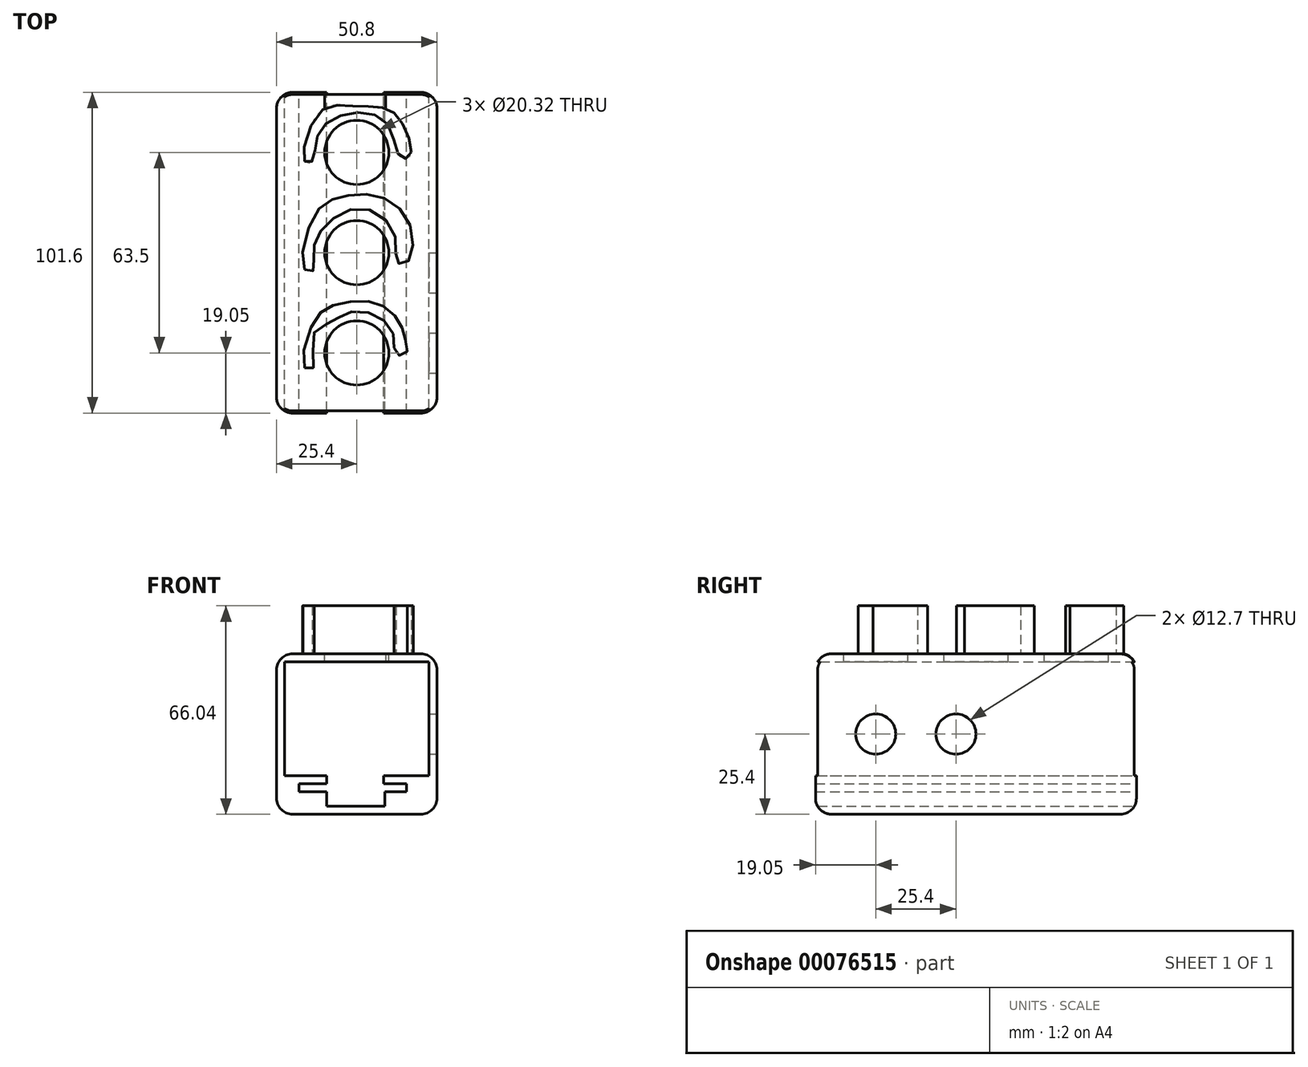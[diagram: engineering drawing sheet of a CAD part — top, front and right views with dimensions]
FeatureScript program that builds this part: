
annotation { "Feature Type Name" : "Feature", "Feature Type Description" : "" }
export const myFeature = defineFeature(function(context is Context, id is Id, definition is map)
    precondition{}
    {
        {
            var Q0;
            Q0=qCreatedBy(makeId("Front.planeOp"),FACE);
            var sketch = newSketch(context, id + "F0", { "sketchPlane" : qUnion([Q0])});
            skLineSegment(sketch, "E0.bottom", {"start": v(-50.8, 50.8) * mm, "end": v(0, 50.8) * mm});
            skLineSegment(sketch, "E0.top", {"start": v(-50.8, 0) * mm, "end": v(0, 0) * mm});
            skLineSegment(sketch, "E0.left", {"start": v(-50.8, 50.8) * mm, "end": v(-50.8, 0) * mm});
            skLineSegment(sketch, "E0.right", {"start": v(0, 50.8) * mm, "end": v(0, 0) * mm});
            skLineSegment(sketch, "E1.0", {"start": v(-48.26, 48.26) * mm, "end": v(-2.54, 48.26) * mm});
            skLineSegment(sketch, "E1.1", {"start": v(-48.26, 48.26) * mm, "end": v(-48.26, 12.2) * mm});
            skLineSegment(sketch, "E1.2", {"start": v(-34.92, 2.54) * mm, "end": v(-16.52, 2.54) * mm});
            skLineSegment(sketch, "E1.3", {"start": v(-2.54, 48.26) * mm, "end": v(-2.54, 12.2) * mm});
            skLineSegment(sketch, "E2", {"start": v(-48.26, 12.2) * mm, "end": v(-34.92, 12.2) * mm});
            skLineSegment(sketch, "E3", {"start": v(-34.92, 12.2) * mm, "end": v(-34.92, 9.65) * mm});
            skLineSegment(sketch, "E4", {"start": v(-34.92, 9.65) * mm, "end": v(-43.69, 9.65) * mm});
            skLineSegment(sketch, "E5", {"start": v(-43.69, 9.65) * mm, "end": v(-43.69, 7.11) * mm});
            skLineSegment(sketch, "E6", {"start": v(-43.69, 7.11) * mm, "end": v(-34.92, 7.11) * mm});
            skLineSegment(sketch, "E7", {"start": v(-34.92, 7.11) * mm, "end": v(-34.92, 2.54) * mm});
            skLineSegment(sketch, "E8", {"start": v(-2.54, 12.2) * mm, "end": v(-16.87, 12.2) * mm});
            skLineSegment(sketch, "E9", {"start": v(-16.87, 12.2) * mm, "end": v(-16.87, 9.65) * mm});
            skLineSegment(sketch, "E10", {"start": v(-16.87, 9.65) * mm, "end": v(-9.65, 9.65) * mm});
            skLineSegment(sketch, "E11", {"start": v(-9.65, 9.65) * mm, "end": v(-9.65, 7.11) * mm});
            skLineSegment(sketch, "E12", {"start": v(-9.65, 7.11) * mm, "end": v(-16.52, 7.11) * mm});
            skLineSegment(sketch, "E13", {"start": v(-16.52, 7.11) * mm, "end": v(-16.52, 2.54) * mm});
            skSolve(sketch);
        }
        {
            var Q0;
            Q0=makeQuery(id+"F0.imprint","IMPRINT",FACE,{"disambiguationData":[TD([[makeQuery(id+"F0.imprint","IMPRINT",EDGE,{"derivedFrom":sQuery(id+"F0.wireOp",EDGE,"E0.bottom")}),-1.0]])]});
            extrude(context, id + "F1", {"entities" : qUnion([Q0]), "depth" : 101.6 * mm});
        }
        {
            var Q0;
            Q0=makeQuery(id+"F1.opExtrude","SWEPT_FACE",FACE,{"disambiguationData":[OSD([sQuery(id+"F0.wireOp",EDGE,"E0.bottom")])]});
            var sketch = newSketch(context, id + "F2", { "sketchPlane" : qUnion([Q0])});
            skCircle(sketch, "E14", {"center": v(-25.4, -19.05) * mm, "radius": 10.16 * mm});
            skCircle(sketch, "E15", {"center": v(-25.4, -50.8) * mm, "radius": 10.16 * mm});
            skCircle(sketch, "E16", {"center": v(-25.4, -82.55) * mm, "radius": 10.16 * mm});
            skLineSegment(sketch, "E17", {"start": v(-25.4, 0) * mm, "end": v(-25.4, -101.6) * mm});
            skLineSegment(sketch, "E18", {"start": v(-26.09, -99.7) * mm, "end": v(-25.4, -101.6) * mm});
            skSolve(sketch);
        }
        {
            var Q0;
            {var subQ0=sQuery(id+"F2.wireOp",EDGE,"E17");var subQ1=sQuery(id+"F2.wireOp",EDGE,"E14");var subQ2=makeQuery(id+"F2.imprint","INTERSECT",VERTEX,{"disambiguationData":[OD(0.0)],"derivedFrom":[subQ1,subQ0]});Q0=makeQuery(id+"F2.imprint","IMPRINT",FACE,{"disambiguationData":[TD([[makeQuery(id+"F2.imprint","IMPRINT",EDGE,{"disambiguationData":[TD([[subQ2,-1.0]])],"derivedFrom":subQ1}),1.0]])]});}
            var Q1;
            {var subQ0=sQuery(id+"F2.wireOp",EDGE,"E17");var subQ1=sQuery(id+"F2.wireOp",EDGE,"E14");var subQ2=makeQuery(id+"F2.imprint","INTERSECT",VERTEX,{"disambiguationData":[OD(0.0)],"derivedFrom":[subQ1,subQ0]});Q1=makeQuery(id+"F2.imprint","IMPRINT",FACE,{"disambiguationData":[TD([[makeQuery(id+"F2.imprint","IMPRINT",EDGE,{"disambiguationData":[TD([[subQ2,1.0]])],"derivedFrom":subQ1}),1.0]])]});}
            var Q2;
            {var subQ0=sQuery(id+"F2.wireOp",EDGE,"E17");var subQ1=sQuery(id+"F2.wireOp",EDGE,"E15");var subQ2=makeQuery(id+"F2.imprint","INTERSECT",VERTEX,{"disambiguationData":[OD(0.0)],"derivedFrom":[subQ1,subQ0]});Q2=makeQuery(id+"F2.imprint","IMPRINT",FACE,{"disambiguationData":[TD([[makeQuery(id+"F2.imprint","IMPRINT",EDGE,{"disambiguationData":[TD([[subQ2,-1.0]])],"derivedFrom":subQ1}),1.0]])]});}
            var Q3;
            {var subQ0=sQuery(id+"F2.wireOp",EDGE,"E17");var subQ1=sQuery(id+"F2.wireOp",EDGE,"E15");var subQ2=makeQuery(id+"F2.imprint","INTERSECT",VERTEX,{"disambiguationData":[OD(0.0)],"derivedFrom":[subQ1,subQ0]});Q3=makeQuery(id+"F2.imprint","IMPRINT",FACE,{"disambiguationData":[TD([[makeQuery(id+"F2.imprint","IMPRINT",EDGE,{"disambiguationData":[TD([[subQ2,1.0]])],"derivedFrom":subQ1}),1.0]])]});}
            var Q4;
            {var subQ0=sQuery(id+"F2.wireOp",EDGE,"E17");var subQ1=sQuery(id+"F2.wireOp",EDGE,"E16");var subQ2=makeQuery(id+"F2.imprint","INTERSECT",VERTEX,{"disambiguationData":[OD(0.0)],"derivedFrom":[subQ1,subQ0]});Q4=makeQuery(id+"F2.imprint","IMPRINT",FACE,{"disambiguationData":[TD([[makeQuery(id+"F2.imprint","IMPRINT",EDGE,{"disambiguationData":[TD([[subQ2,-1.0]])],"derivedFrom":subQ1}),1.0]])]});}
            var Q5;
            {var subQ0=sQuery(id+"F2.wireOp",EDGE,"E17");var subQ1=sQuery(id+"F2.wireOp",EDGE,"E16");var subQ2=makeQuery(id+"F2.imprint","INTERSECT",VERTEX,{"disambiguationData":[OD(0.0)],"derivedFrom":[subQ1,subQ0]});Q5=makeQuery(id+"F2.imprint","IMPRINT",FACE,{"disambiguationData":[TD([[makeQuery(id+"F2.imprint","IMPRINT",EDGE,{"disambiguationData":[TD([[subQ2,1.0]])],"derivedFrom":subQ1}),1.0]])]});}
            extrude(context, id + "F3", {"entities" : qUnion([Q0, Q1, Q2, Q3, Q4, Q5]), "operationType" : NewBodyOperationType.REMOVE, "oppositeDirection" : true, "depth" : 25.4 * mm});
        }
        {
            var Q0;
            Q0=makeQuery(id+"F1.opExtrude","SWEPT_FACE",FACE,{"disambiguationData":[OSD([sQuery(id+"F0.wireOp",EDGE,"E0.right")])]});
            var sketch = newSketch(context, id + "F4", { "sketchPlane" : qUnion([Q0])});
            skLineSegment(sketch, "E19", {"start": v(0, 25.4) * mm, "end": v(-101.6, 25.4) * mm});
            skCircle(sketch, "E20", {"center": v(-82.55, 25.4) * mm, "radius": 6.35 * mm});
            skCircle(sketch, "E21", {"center": v(-57.15, 25.4) * mm, "radius": 6.35 * mm});
            skSolve(sketch);
        }
        {
            var Q0;
            {var subQ0=sQuery(id+"F4.wireOp",EDGE,"E20");var subQ1=sQuery(id+"F4.wireOp",EDGE,"E19");var subQ2=makeQuery(id+"F4.imprint","INTERSECT",VERTEX,{"disambiguationData":[OD(0.0)],"derivedFrom":[subQ1,subQ0]});Q0=makeQuery(id+"F4.imprint","IMPRINT",FACE,{"disambiguationData":[TD([[makeQuery(id+"F4.imprint","IMPRINT",EDGE,{"disambiguationData":[TD([[subQ2,-1.0]])],"derivedFrom":subQ1}),1.0]])]});}
            var Q1;
            {var subQ0=sQuery(id+"F4.wireOp",EDGE,"E20");var subQ1=sQuery(id+"F4.wireOp",EDGE,"E19");var subQ2=makeQuery(id+"F4.imprint","INTERSECT",VERTEX,{"disambiguationData":[OD(0.0)],"derivedFrom":[subQ1,subQ0]});Q1=makeQuery(id+"F4.imprint","IMPRINT",FACE,{"disambiguationData":[TD([[makeQuery(id+"F4.imprint","IMPRINT",EDGE,{"disambiguationData":[TD([[subQ2,-1.0]])],"derivedFrom":subQ1}),-1.0]])]});}
            var Q2;
            {var subQ0=sQuery(id+"F4.wireOp",EDGE,"E21");var subQ1=sQuery(id+"F4.wireOp",EDGE,"E19");var subQ2=makeQuery(id+"F4.imprint","INTERSECT",VERTEX,{"disambiguationData":[OD(0.0)],"derivedFrom":[subQ1,subQ0]});Q2=makeQuery(id+"F4.imprint","IMPRINT",FACE,{"disambiguationData":[TD([[makeQuery(id+"F4.imprint","IMPRINT",EDGE,{"disambiguationData":[TD([[subQ2,-1.0]])],"derivedFrom":subQ1}),-1.0]])]});}
            var Q3;
            {var subQ0=sQuery(id+"F4.wireOp",EDGE,"E21");var subQ1=sQuery(id+"F4.wireOp",EDGE,"E19");var subQ2=makeQuery(id+"F4.imprint","INTERSECT",VERTEX,{"disambiguationData":[OD(0.0)],"derivedFrom":[subQ1,subQ0]});Q3=makeQuery(id+"F4.imprint","IMPRINT",FACE,{"disambiguationData":[TD([[makeQuery(id+"F4.imprint","IMPRINT",EDGE,{"disambiguationData":[TD([[subQ2,-1.0]])],"derivedFrom":subQ1}),1.0]])]});}
            extrude(context, id + "F5", {"entities" : qUnion([Q0, Q1, Q2, Q3]), "operationType" : NewBodyOperationType.REMOVE, "oppositeDirection" : true, "depth" : 25.4 * mm});
        }
        {
            var Q0;
            Q0=makeQuery(id+"F1.opExtrude","SWEPT_FACE",FACE,{"disambiguationData":[OSD([sQuery(id+"F0.wireOp",EDGE,"E0.bottom")])]});
            var sketch = newSketch(context, id + "F6", { "sketchPlane" : qUnion([Q0])});
            skFitSpline(sketch, "E22", {"points": [v(-41.88, -21.9) * mm, v(-39.44, -21.73) * mm, v(-37.62, -13.22) * mm, v(-27.55, -6.68) * mm, v(-15.71, -9.95) * mm, v(-11.75, -20.28) * mm, v(-8.63, -20.35) * mm, v(-9.94, -11.77) * mm, v(-15.76, -5.26) * mm, v(-26.01, -4.37) * mm, v(-36.95, -6.16) * mm, v(-41.88, -21.9) * mm]});
            skPoint(sketch, "E23.2.internal.snap0", {"position": v(-50.8, -50.8) * mm});
            skFitSpline(sketch, "E23", {"points": [v(-41.88, -56.16) * mm, v(-39.24, -56.54) * mm, v(-39.14, -50.8) * mm, v(-35.46, -42.26) * mm, v(-23.31, -36.74) * mm, v(-13.33, -45.29) * mm, v(-12.7, -53.63) * mm, v(-9.4, -53.84) * mm, v(-8.42, -42.36) * mm, v(-17.83, -33.09) * mm, v(-30.28, -33.14) * mm, v(-38.8, -38.82) * mm, v(-41.88, -56.16) * mm]});
            skFitSpline(sketch, "E24", {"points": [v(-41.88, -87.33) * mm, v(-39.24, -87.4) * mm, v(-39.24, -76.83) * mm, v(-33.16, -72.58) * mm, v(-27.6, -69.57) * mm, v(-18.24, -71.23) * mm, v(-13.53, -78.05) * mm, v(-13.17, -82.7) * mm, v(-9.87, -82.9) * mm, v(-9.8, -79.17) * mm, v(-11.17, -74.33) * mm, v(-15.41, -68.74) * mm, v(-23.41, -66.09) * mm, v(-33.7, -67.8) * mm, v(-39.24, -73.12) * mm, v(-41.88, -87.33) * mm]});
            skSolve(sketch);
        }
        {
            var Q0;
            Q0=makeQuery(id+"F6.imprint","IMPRINT",FACE,{"disambiguationData":[TD([[makeQuery(id+"F6.imprint","IMPRINT",EDGE,{"derivedFrom":sQuery(id+"F6.wireOp",EDGE,"E22")}),1.0]])]});
            var Q1;
            Q1=makeQuery(id+"F6.imprint","IMPRINT",FACE,{"disambiguationData":[TD([[makeQuery(id+"F6.imprint","IMPRINT",EDGE,{"derivedFrom":sQuery(id+"F6.wireOp",EDGE,"E23")}),1.0]])]});
            var Q2;
            Q2=makeQuery(id+"F6.imprint","IMPRINT",FACE,{"disambiguationData":[TD([[makeQuery(id+"F6.imprint","IMPRINT",EDGE,{"derivedFrom":sQuery(id+"F6.wireOp",EDGE,"E24")}),1.0]])]});
            extrude(context, id + "F7", {"entities" : qUnion([Q0, Q1, Q2]), "operationType" : NewBodyOperationType.ADD, "depth" : 15.24 * mm});
        }
        {
            var Q0;
            Q0=makeQuery(id+"F1.opExtrude","SWEPT_EDGE",EDGE,{"disambiguationData":[OSD([sQuery(id+"F0.wireOp",EDGE,"E0.bottom"),sQuery(id+"F0.wireOp",EDGE,"E0.left")])]});
            var Q1;
            Q1=makeQuery(id+"F1.opExtrude","SWEPT_EDGE",EDGE,{"disambiguationData":[OSD([sQuery(id+"F0.wireOp",EDGE,"E0.top"),sQuery(id+"F0.wireOp",EDGE,"E0.left")])]});
            var Q2;
            Q2=makeQuery(id+"F1.opExtrude","SWEPT_EDGE",EDGE,{"disambiguationData":[OSD([sQuery(id+"F0.wireOp",EDGE,"E0.bottom"),sQuery(id+"F0.wireOp",EDGE,"E0.right")])]});
            fillet(context, id + "F8", {"entities" : qUnion([Q0, Q1, Q2]), "radius" : 5.08 * mm, "tangentPropagation" : true, "allowEdgeOverflow" : false});
        }
        {
            var Q0;
            Q0=makeQuery(id+"F1.opExtrude","SWEPT_EDGE",EDGE,{"disambiguationData":[OSD([sQuery(id+"F0.wireOp",EDGE,"E0.top"),sQuery(id+"F0.wireOp",EDGE,"E0.right")])]});
            var Q1;
            Q1=makeQuery(id+"F1.opExtrude","CAP_EDGE",EDGE,{"disambiguationData":[OSD([sQuery(id+"F0.wireOp",EDGE,"E0.top")])],"isStart":true});
            fillet(context, id + "F9", {"entities" : qUnion([Q0, Q1]), "radius" : 5.08 * mm, "tangentPropagation" : true, "allowEdgeOverflow" : false});
        }
        {
            var Q0;
            Q0=makeQuery(id+"F1.opExtrude","CAP_EDGE",EDGE,{"disambiguationData":[OSD([sQuery(id+"F0.wireOp",EDGE,"E0.left")])],"isStart":false});
            fillet(context, id + "F10", {"entities" : qUnion([Q0]), "radius" : 5.08 * mm, "tangentPropagation" : true, "allowEdgeOverflow" : false});
        }
    });
